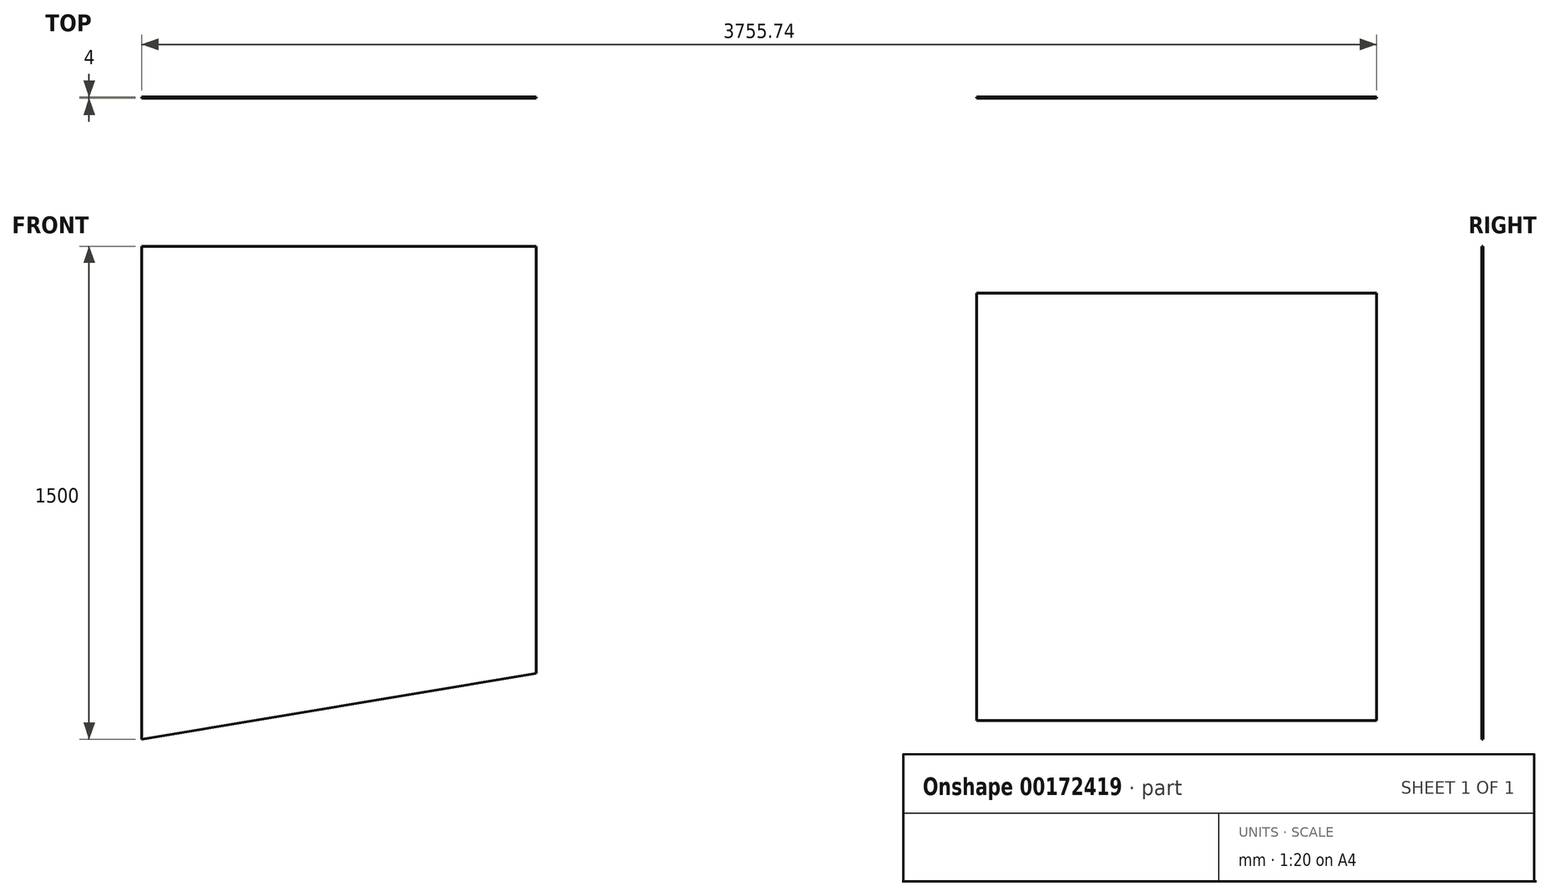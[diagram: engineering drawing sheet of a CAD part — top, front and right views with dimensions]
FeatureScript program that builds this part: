
annotation { "Feature Type Name" : "Feature", "Feature Type Description" : "" }
export const myFeature = defineFeature(function(context is Context, id is Id, definition is map)
    precondition{}
    {
        {
            var Q0;
            Q0=qCreatedBy(makeId("Front.planeOp"),FACE);
            var sketch = newSketch(context, id + "F0", { "sketchPlane" : qUnion([Q0])});
            skLineSegment(sketch, "E0", {"start": v(-789.1, 913.92) * mm, "end": v(410.9, 913.92) * mm});
            skLineSegment(sketch, "E1", {"start": v(410.9, 913.92) * mm, "end": v(410.9, -386.08) * mm});
            skLineSegment(sketch, "E2", {"start": v(410.9, -386.08) * mm, "end": v(-789.1, -586.08) * mm});
            skLineSegment(sketch, "E3", {"start": v(-789.1, -586.08) * mm, "end": v(-789.1, 913.92) * mm});
            skLineSegment(sketch, "E4.bottom", {"start": v(1750.08, 771.09) * mm, "end": v(2966.64, 771.09) * mm});
            skLineSegment(sketch, "E4.top", {"start": v(1750.08, -528.91) * mm, "end": v(2966.64, -528.91) * mm});
            skLineSegment(sketch, "E4.left", {"start": v(1750.08, 771.09) * mm, "end": v(1750.08, -528.91) * mm});
            skLineSegment(sketch, "E4.right", {"start": v(2966.64, 771.09) * mm, "end": v(2966.64, -528.91) * mm});
            skSolve(sketch);
        }
        {
            var Q0;
            Q0=makeQuery(id+"F0.imprint","IMPRINT",FACE,{"disambiguationData":[TD([[makeQuery(id+"F0.imprint","IMPRINT",EDGE,{"derivedFrom":sQuery(id+"F0.wireOp",EDGE,"E0")}),-1.0]])]});
            extrude(context, id + "F1", {"entities" : qUnion([Q0]), "depth" : 4 * mm});
        }
        {
            var Q0;
            Q0=makeQuery(id+"F0.imprint","IMPRINT",FACE,{"disambiguationData":[TD([[makeQuery(id+"F0.imprint","IMPRINT",EDGE,{"derivedFrom":sQuery(id+"F0.wireOp",EDGE,"E4.bottom")}),-1.0]])]});
            extrude(context, id + "F2", {"entities" : qUnion([Q0]), "depth" : 4 * mm});
        }
    });
